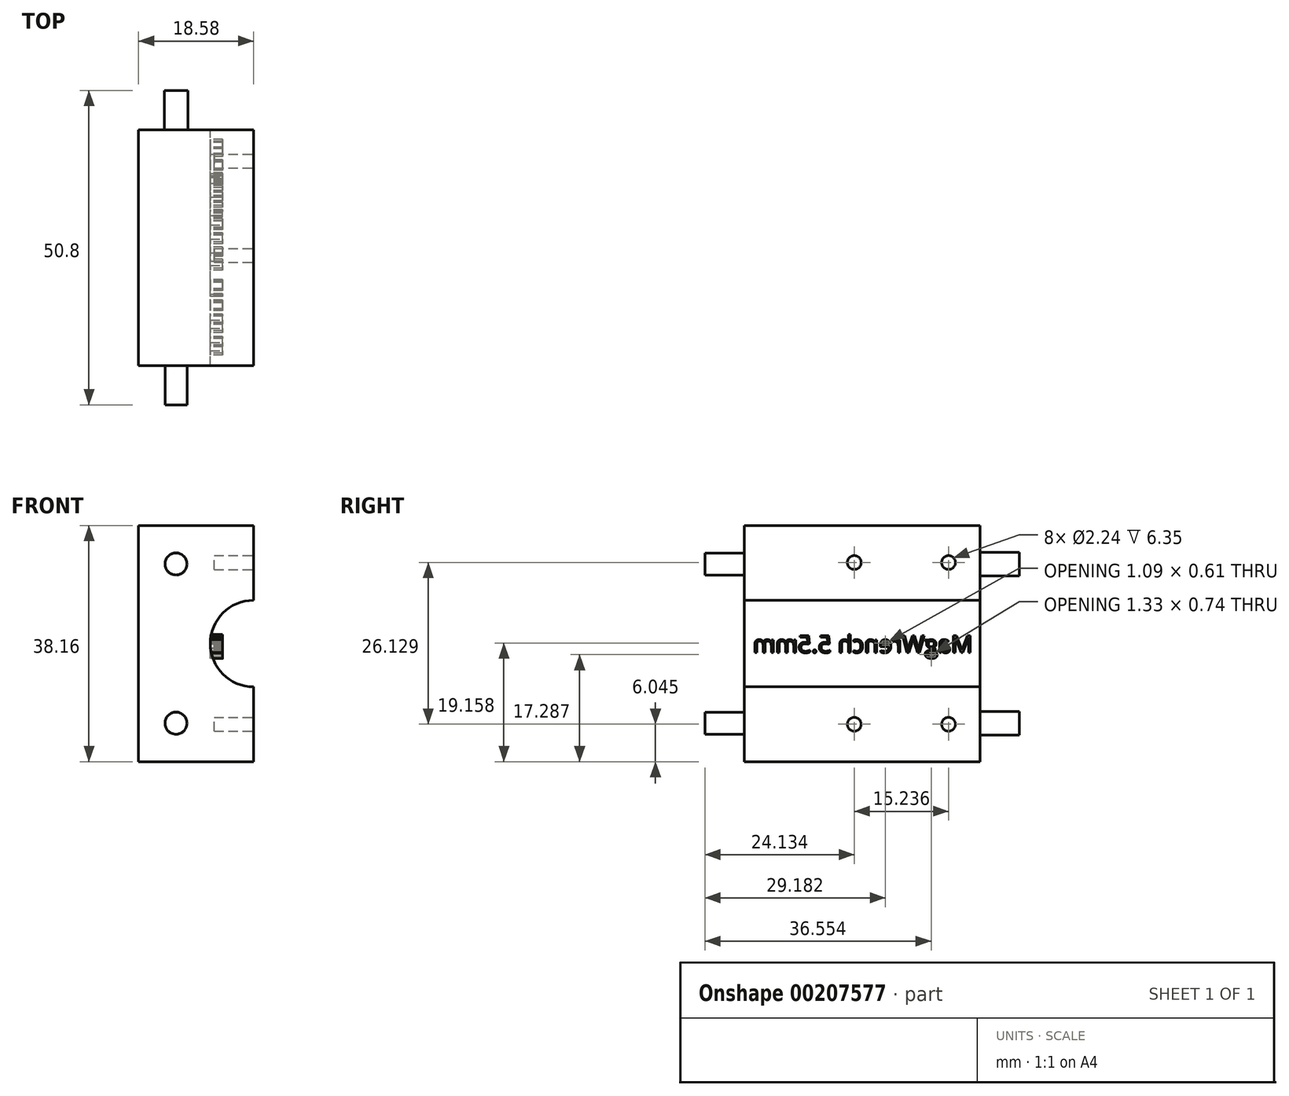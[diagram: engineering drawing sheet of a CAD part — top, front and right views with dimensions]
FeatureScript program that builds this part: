
annotation { "Feature Type Name" : "Feature", "Feature Type Description" : "" }
export const myFeature = defineFeature(function(context is Context, id is Id, definition is map)
    precondition{}
    {
        {
            var Q0;
            Q0=qCreatedBy(makeId("Front.planeOp"),FACE);
            var sketch = newSketch(context, id + "F0", { "sketchPlane" : qUnion([Q0])});
            skArc(sketch, "E0", {"start": v(0, 6.99) * mm, "mid": v(-6.99, 0) * mm, "end": v(0, -6.99) * mm});
            skLineSegment(sketch, "E1.bottom", {"start": v(0, 19.08) * mm, "end": v(-18.58, 19.08) * mm});
            skLineSegment(sketch, "E1.top", {"start": v(0, -19.08) * mm, "end": v(-18.58, -19.08) * mm});
            skLineSegment(sketch, "E1.left", {"start": v(0, 19.08) * mm, "end": v(0, 6.99) * mm});
            skLineSegment(sketch, "E1.right", {"start": v(-18.58, 19.08) * mm, "end": v(-18.58, -19.08) * mm});
            skPoint(sketch, "E2", {"position": v(0, 6.99) * mm});
            skPoint(sketch, "E3", {"position": v(0, -6.99) * mm});
            skLineSegment(sketch, "E4.trimOffspring", {"start": v(0, -6.99) * mm, "end": v(0, -19.08) * mm});
            skPoint(sketch, "E5", {"position": v(-6.99, 0) * mm});
            skSolve(sketch);
        }
        {
            var Q0;
            Q0 = qSketchRegion(id + "F0", true);
            extrude(context, id + "F1", {"entities" : qUnion([Q0]), "depth" : 38.1 * mm});
        }
        {
            var Q0;
            Q0=qCreatedBy(makeId("Right.planeOp"),FACE);
            var sketch = newSketch(context, id + "F2", { "sketchPlane" : qUnion([Q0])});
            skLineSegment(sketch, "E6", {"start": v(-25.4, 7.04) * mm, "end": v(-25.4, 19.15) * mm, "construction": true});
            skLineSegment(sketch, "E7", {"start": v(-25.4, 13.1) * mm, "end": v(0, 13.1) * mm, "construction": true});
            skCircle(sketch, "E8", {"center": v(-20.32, 13.1) * mm, "radius": 1.12 * mm});
            skCircle(sketch, "E9", {"center": v(-5.08, 13.1) * mm, "radius": 1.12 * mm});
            skLineSegment(sketch, "E10", {"start": v(-25.43, -6.98) * mm, "end": v(-25.43, -19.1) * mm, "construction": true});
            skLineSegment(sketch, "E11", {"start": v(-25.43, -13.04) * mm, "end": v(0, -13.04) * mm, "construction": true});
            skCircle(sketch, "E12", {"center": v(-20.32, -13.04) * mm, "radius": 1.12 * mm});
            skCircle(sketch, "E13", {"center": v(-5.08, -13.04) * mm, "radius": 1.12 * mm});
            skLineSegment(sketch, "E14", {"start": v(-25.4, 13.1) * mm, "end": v(-20.32, 13.1) * mm, "construction": true});
            skSolve(sketch);
        }
        {
            var Q0;
            Q0 = qSketchRegion(id + "F2", true);
            extrude(context, id + "F3", {"entities" : qUnion([Q0]), "operationType" : NewBodyOperationType.REMOVE, "oppositeDirection" : true, "depth" : 6.35 * mm});
        }
        {
            var Q0;
            Q0=makeQuery(id+"F1.opExtrude","SWEPT_BODY",BODY,{"disambiguationData":[OSD([sQuery(id+"F0.wireOp",EDGE,"E0"),sQuery(id+"F0.wireOp",EDGE,"E1.bottom"),sQuery(id+"F0.wireOp",EDGE,"E1.top"),sQuery(id+"F0.wireOp",EDGE,"E1.right"),sQuery(id+"F0.wireOp",EDGE,"E1.left"),sQuery(id+"F0.wireOp",EDGE,"E4.trimOffspring")])]});
            transform(context, id + "F4", {"entities" : qUnion([Q0]), "transformType" : TransformType.TRANSLATION_3D, "dx" : 0 * mm, "dy" : 0 * mm, "dz" : 0 * mm, "makeCopy" : true});
        }
        {
            var Q0;
            Q0=makeQuery(id+"F1.opExtrude","CAP_FACE",FACE,{"disambiguationData":[OSD([sQuery(id+"F0.wireOp",EDGE,"E0"),sQuery(id+"F0.wireOp",EDGE,"E1.bottom"),sQuery(id+"F0.wireOp",EDGE,"E1.top"),sQuery(id+"F0.wireOp",EDGE,"E1.right"),sQuery(id+"F0.wireOp",EDGE,"E1.left"),sQuery(id+"F0.wireOp",EDGE,"E4.trimOffspring")])],"isStart":false});
            var sketch = newSketch(context, id + "F5", { "sketchPlane" : qUnion([Q0])});
            skLineSegment(sketch, "E15", {"start": v(-18.58, 19.08) * mm, "end": v(0, 0) * mm, "construction": true});
            skLineSegment(sketch, "E16", {"start": v(0, 0) * mm, "end": v(-18.58, -19.08) * mm, "construction": true});
            skCircle(sketch, "E17", {"center": v(0, 0) * mm, "radius": 17.96 * mm, "construction": true});
            skCircle(sketch, "E18", {"center": v(-12.53, 12.86) * mm, "radius": 1.78 * mm});
            skCircle(sketch, "E19", {"center": v(-12.53, -12.86) * mm, "radius": 1.78 * mm});
            skSolve(sketch);
        }
        {
            var Q0;
            Q0=makeQuery(id+"F5.imprint","IMPRINT",FACE,{"disambiguationData":[TD([[makeQuery(id+"F5.imprint","IMPRINT",EDGE,{"derivedFrom":sQuery(id+"F5.wireOp",EDGE,"E18")}),1.0]])]});
            var Q1;
            Q1=makeQuery(id+"F5.imprint","IMPRINT",FACE,{"disambiguationData":[TD([[makeQuery(id+"F5.imprint","IMPRINT",EDGE,{"derivedFrom":sQuery(id+"F5.wireOp",EDGE,"E19")}),1.0]])]});
            extrude(context, id + "F6", {"entities" : qUnion([Q0, Q1]), "depth" : 6.35 * mm});
        }
        {
            var Q0;
            Q0=makeQuery(id+"F1.opExtrude","CAP_FACE",FACE,{"disambiguationData":[OSD([sQuery(id+"F0.wireOp",EDGE,"E0"),sQuery(id+"F0.wireOp",EDGE,"E1.bottom"),sQuery(id+"F0.wireOp",EDGE,"E1.top"),sQuery(id+"F0.wireOp",EDGE,"E1.right"),sQuery(id+"F0.wireOp",EDGE,"E1.left"),sQuery(id+"F0.wireOp",EDGE,"E4.trimOffspring")])],"isStart":true});
            var sketch = newSketch(context, id + "F7", { "sketchPlane" : qUnion([Q0])});
            skLineSegment(sketch, "E20", {"start": v(18.58, 19.08) * mm, "end": v(0, 0) * mm, "construction": true});
            skLineSegment(sketch, "E21", {"start": v(0, 0) * mm, "end": v(18.58, -19.08) * mm, "construction": true});
            skCircle(sketch, "E22", {"center": v(0, 0) * mm, "radius": 17.96 * mm, "construction": true});
            skCircle(sketch, "E23", {"center": v(12.53, 12.86) * mm, "radius": 1.9 * mm});
            skCircle(sketch, "E24", {"center": v(12.53, -12.86) * mm, "radius": 1.9 * mm});
            skSolve(sketch);
        }
        {
            var Q0;
            Q0=makeQuery(id+"F7.imprint","IMPRINT",FACE,{"disambiguationData":[TD([[makeQuery(id+"F7.imprint","IMPRINT",EDGE,{"derivedFrom":sQuery(id+"F7.wireOp",EDGE,"E23")}),1.0]])]});
            var Q1;
            Q1=makeQuery(id+"F7.imprint","IMPRINT",FACE,{"disambiguationData":[TD([[makeQuery(id+"F7.imprint","IMPRINT",EDGE,{"derivedFrom":sQuery(id+"F7.wireOp",EDGE,"E24")}),1.0]])]});
            extrude(context, id + "F8", {"entities" : qUnion([Q0, Q1]), "depth" : 6.35 * mm});
        }
        {
            var Q0;
            Q0=makeQuery(id+"F1.opExtrude","CAP_EDGE",EDGE,{"disambiguationData":[OSD([sQuery(id+"F0.wireOp",EDGE,"E0")])],"isStart":false});
            cPoint(context, id + "F9", {"entities" : qUnion([Q0]), "parameter" : 0.5});
        }
        {
            var Q0;
            Q0 = qCreatedBy(id + "F9" ,VERTEX);
            var Q1;
            Q1=qCreatedBy(makeId("Right.planeOp"),FACE);
            cPlane(context, id + "F10", {"entities" : qUnion([Q0, Q1]), "cplaneType" : CPlaneType.PLANE_POINT, "offset" : 25.4 * mm, "width" : 152.4 * mm, "height" : 152.4 * mm});
        }
        {
            var Q0;
            Q0=qCreatedBy(id+"F10.planeOp",FACE);
            var sketch = newSketch(context, id + "F11", { "sketchPlane" : qUnion([Q0])});
            skLineSegment(sketch, "E25", {"start": v(-19.7, 12.83) * mm, "end": v(-19.7, -8.71) * mm, "construction": true});
            skSolve(sketch);
        }
        {
            var Q0;
            Q0=qCreatedBy(id+"F10.planeOp",FACE);
            var Q1;
            Q1=sQuery(id+"F11.wireOp",EDGE,"E25");
            cPlane(context, id + "F12", {"entities" : qUnion([Q0, Q1]), "cplaneType" : CPlaneType.LINE_ANGLE, "offset" : 25.4 * mm, "angle" : 0 * degree, "width" : 152.4 * mm, "height" : 152.4 * mm});
        }
        {
            var Q0;
            Q0=qCreatedBy(id+"F12.planeOp",FACE);
            var sketch = newSketch(context, id + "F13", { "sketchPlane" : qUnion([Q0])});
            skText(sketch, "E26", { "text": "MagWrench 5.5mm", "fontName": "OpenSans-Regular.ttf"});
            const initialGuessF13  = {"E26": [0.00118, -0.00147, 1, 0, 0.0028]};
            skSetInitialGuess(sketch, initialGuessF13);
            skSolve(sketch);
        }
        {
            var Q0;
            Q0 = qSketchRegion(id + "F13", true);
            extrude(context, id + "F14", {"entities" : qUnion([Q0]), "oppositeDirection" : true, "depth" : 2 * mm});
        }
    });
